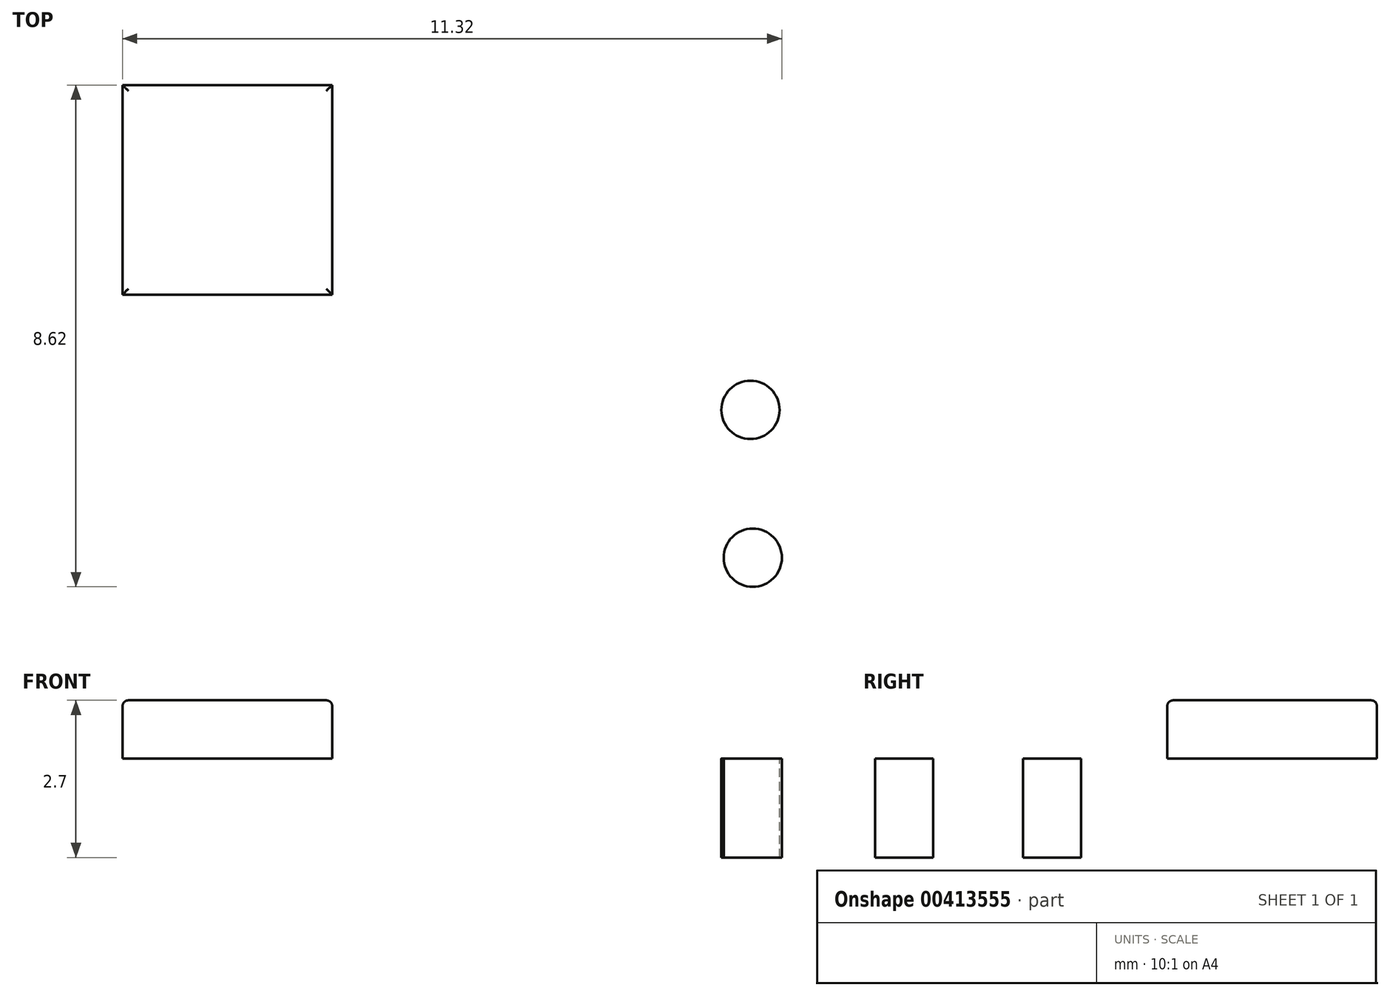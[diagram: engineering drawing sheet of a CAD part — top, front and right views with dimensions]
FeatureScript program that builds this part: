
annotation { "Feature Type Name" : "Feature", "Feature Type Description" : "" }
export const myFeature = defineFeature(function(context is Context, id is Id, definition is map)
    precondition{}
    {
        {
            var Q0;
            Q0=qCreatedBy(makeId("Top.planeOp"),FACE);
            var sketch = newSketch(context, id + "F0", { "sketchPlane" : qUnion([Q0])});
            skLineSegment(sketch, "E0.bottom", {"start": v(6.6, 5.3) * mm, "end": v(-6.6, 5.3) * mm});
            skLineSegment(sketch, "E0.top", {"start": v(6.6, -5.3) * mm, "end": v(-6.6, -5.3) * mm});
            skLineSegment(sketch, "E0.left", {"start": v(6.6, 5.3) * mm, "end": v(6.6, -5.3) * mm});
            skLineSegment(sketch, "E0.right", {"start": v(-6.6, 5.3) * mm, "end": v(-6.6, -5.3) * mm});
            skPoint(sketch, "E0.middle", {"position": v(0, 0) * mm});
            skSolve(sketch);
        }
        {
            var Q0;
            Q0 = qSketchRegion(id + "F0", true);
            extrude(context, id + "F1", {"entities" : qUnion([Q0]), "depth" : 1.7 * mm});
        }
        {
            var Q0;
            Q0=makeQuery(id+"F1.opExtrude","CAP_FACE",FACE,{"disambiguationData":[OSD([sQuery(id+"F0.wireOp",EDGE,"E0.bottom"),sQuery(id+"F0.wireOp",EDGE,"E0.top"),sQuery(id+"F0.wireOp",EDGE,"E0.left"),sQuery(id+"F0.wireOp",EDGE,"E0.right")])],"isStart":false});
            var sketch = newSketch(context, id + "F2", { "sketchPlane" : qUnion([Q0])});
            skCircle(sketch, "E1", {"center": v(5.22, 3.8) * mm, "radius": 0.5 * mm});
            skCircle(sketch, "E2", {"center": v(5.18, 1.27) * mm, "radius": 0.5 * mm});
            skCircle(sketch, "E3.MirrorC", {"center": v(5.18, -1.27) * mm, "radius": 0.5 * mm});
            skCircle(sketch, "E4.MirrorC", {"center": v(5.22, -3.8) * mm, "radius": 0.5 * mm});
            skCircle(sketch, "E5", {"center": v(-4.1, -2.81) * mm, "radius": 1.5 * mm});
            skSolve(sketch);
        }
        {
            var Q0;
            Q0=makeQuery(id+"F2.imprint","IMPRINT",FACE,{"disambiguationData":[TD([[makeQuery(id+"F2.imprint","IMPRINT",EDGE,{"derivedFrom":sQuery(id+"F2.wireOp",EDGE,"E1")}),1.0]])]});
            var Q1;
            Q1=makeQuery(id+"F2.imprint","IMPRINT",FACE,{"disambiguationData":[TD([[makeQuery(id+"F2.imprint","IMPRINT",EDGE,{"derivedFrom":sQuery(id+"F2.wireOp",EDGE,"E2")}),1.0]])]});
            var Q2;
            Q2=makeQuery(id+"F2.imprint","IMPRINT",FACE,{"disambiguationData":[TD([[makeQuery(id+"F2.imprint","IMPRINT",EDGE,{"derivedFrom":sQuery(id+"F2.wireOp",EDGE,"E3.MirrorC")}),-1.0]])]});
            var Q3;
            Q3=makeQuery(id+"F2.imprint","IMPRINT",FACE,{"disambiguationData":[TD([[makeQuery(id+"F2.imprint","IMPRINT",EDGE,{"derivedFrom":sQuery(id+"F2.wireOp",EDGE,"E4.MirrorC")}),-1.0]])]});
            var Q4;
            Q4=makeQuery(id+"F2.imprint","IMPRINT",FACE,{"disambiguationData":[TD([[makeQuery(id+"F2.imprint","IMPRINT",EDGE,{"derivedFrom":sQuery(id+"F2.wireOp",EDGE,"E5")}),1.0]])]});
            extrude(context, id + "F3", {"entities" : qUnion([Q0, Q1, Q2, Q3, Q4]), "operationType" : NewBodyOperationType.REMOVE, "endBound" : BoundingType.THROUGH_ALL, "oppositeDirection" : true, "depth" : 25 * mm});
        }
        {
            var Q0;
            Q0=makeQuery(id+"F1.opExtrude","CAP_FACE",FACE,{"disambiguationData":[OSD([sQuery(id+"F0.wireOp",EDGE,"E0.bottom"),sQuery(id+"F0.wireOp",EDGE,"E0.top"),sQuery(id+"F0.wireOp",EDGE,"E0.left"),sQuery(id+"F0.wireOp",EDGE,"E0.right")])],"isStart":false});
            var sketch = newSketch(context, id + "F4", { "sketchPlane" : qUnion([Q0])});
            skLineSegment(sketch, "E6.bottom", {"start": v(-5.6, 4.3) * mm, "end": v(-2, 4.3) * mm});
            skLineSegment(sketch, "E6.top", {"start": v(-5.6, 0.7) * mm, "end": v(-2, 0.7) * mm});
            skLineSegment(sketch, "E6.left", {"start": v(-5.6, 4.3) * mm, "end": v(-5.6, 0.7) * mm});
            skLineSegment(sketch, "E6.right", {"start": v(-2, 4.3) * mm, "end": v(-2, 0.7) * mm});
            skSolve(sketch);
        }
        {
            var Q0;
            Q0=makeQuery(id+"F4.imprint","IMPRINT",FACE,{"disambiguationData":[TD([[makeQuery(id+"F4.imprint","IMPRINT",EDGE,{"derivedFrom":sQuery(id+"F4.wireOp",EDGE,"E6.bottom")}),-1.0]])]});
            extrude(context, id + "F5", {"entities" : qUnion([Q0]), "operationType" : NewBodyOperationType.ADD, "depth" : 1 * mm});
        }
        {
            var Q0;
            Q0=makeQuery(id+"F5.opExtrude","CAP_EDGE",EDGE,{"disambiguationData":[OSD([sQuery(id+"F4.wireOp",EDGE,"E6.top")])],"isStart":false});
            var Q1;
            Q1=makeQuery(id+"F5.opExtrude","CAP_EDGE",EDGE,{"disambiguationData":[OSD([sQuery(id+"F4.wireOp",EDGE,"E6.right")])],"isStart":false});
            var Q2;
            Q2=makeQuery(id+"F5.opExtrude","CAP_EDGE",EDGE,{"disambiguationData":[OSD([sQuery(id+"F4.wireOp",EDGE,"E6.left")])],"isStart":false});
            var Q3;
            Q3=makeQuery(id+"F5.opExtrude","CAP_EDGE",EDGE,{"disambiguationData":[OSD([sQuery(id+"F4.wireOp",EDGE,"E6.bottom")])],"isStart":false});
            fillet(context, id + "F6", {"entities" : qUnion([Q0, Q1, Q2, Q3]), "radius" : 0.1 * mm, "tangentPropagation" : true, "allowEdgeOverflow" : false});
        }
    });
